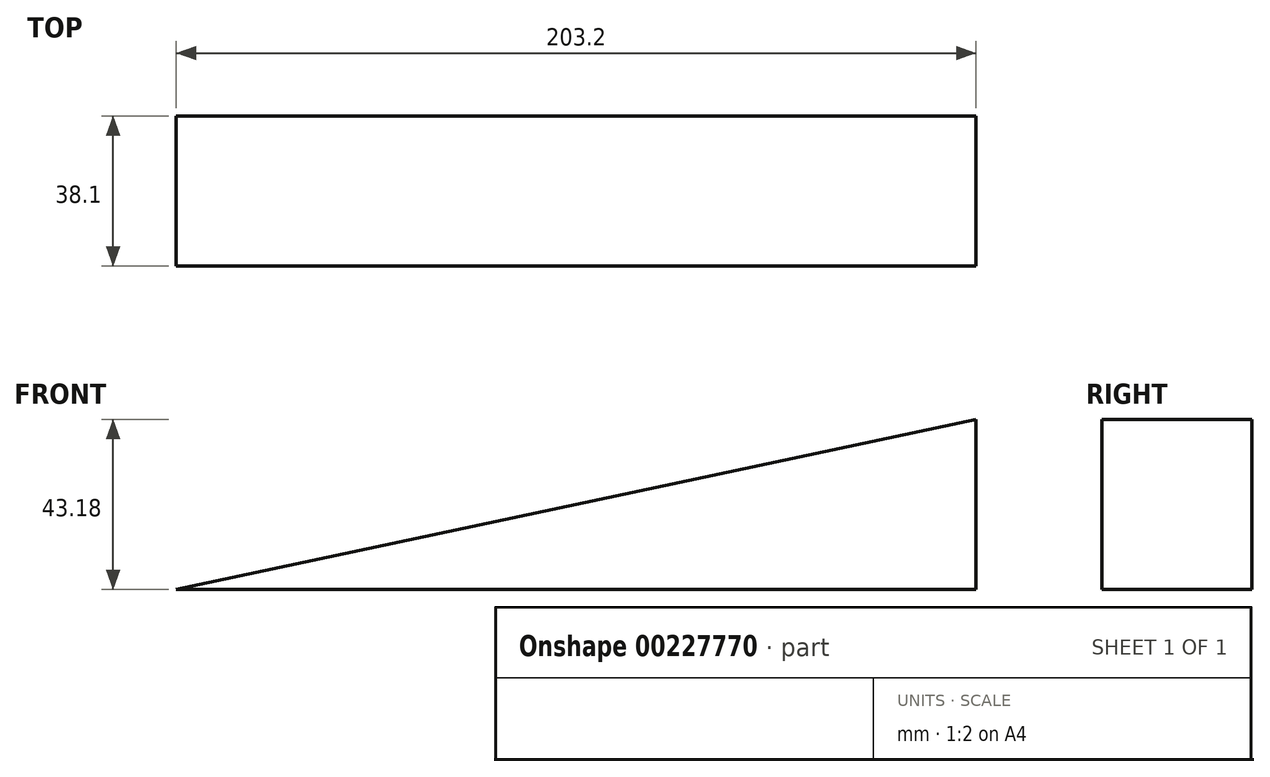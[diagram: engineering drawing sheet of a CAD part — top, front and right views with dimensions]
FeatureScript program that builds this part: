
annotation { "Feature Type Name" : "Feature", "Feature Type Description" : "" }
export const myFeature = defineFeature(function(context is Context, id is Id, definition is map)
    precondition{}
    {
        {
            var Q0;
            Q0=qCreatedBy(makeId("Front.planeOp"),FACE);
            var sketch = newSketch(context, id + "F0", { "sketchPlane" : qUnion([Q0])});
            skLineSegment(sketch, "E0", {"start": v(-99.4, 0) * mm, "end": v(103.8, 0) * mm});
            skLineSegment(sketch, "E1", {"start": v(103.8, 0) * mm, "end": v(103.8, 43.18) * mm});
            skLineSegment(sketch, "E2", {"start": v(103.8, 43.18) * mm, "end": v(-99.4, 0) * mm});
            skSolve(sketch);
        }
        {
            var Q0;
            Q0 = qSketchRegion(id + "F0", true);
            extrude(context, id + "F1", {"entities" : qUnion([Q0]), "depth" : 38.1 * mm});
        }
    });
